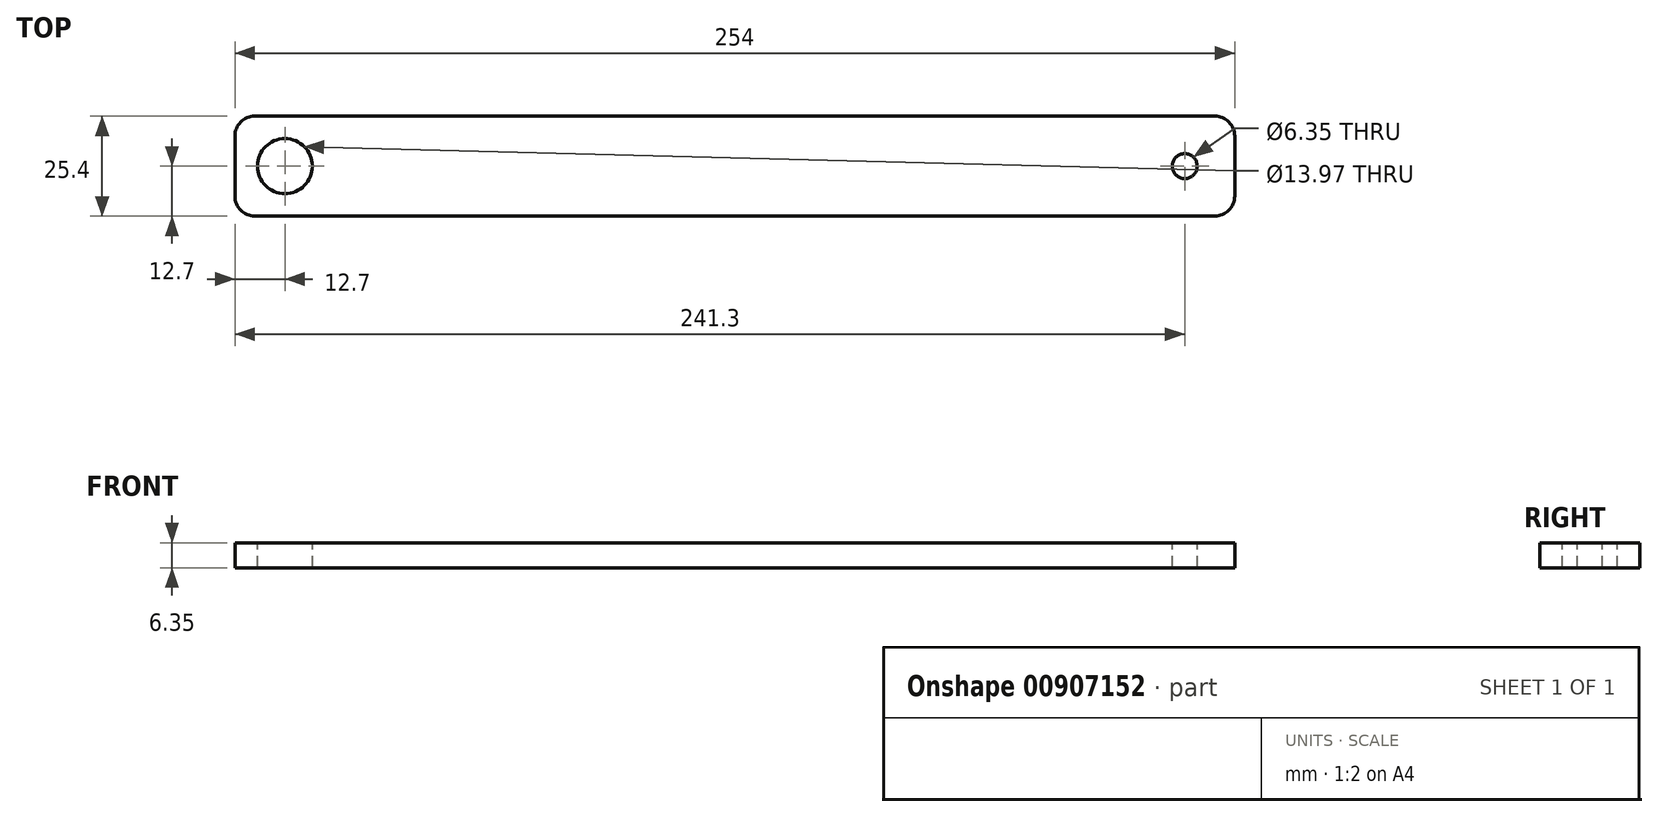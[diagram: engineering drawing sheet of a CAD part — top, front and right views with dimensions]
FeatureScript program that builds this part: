
annotation { "Feature Type Name" : "Feature", "Feature Type Description" : "" }
export const myFeature = defineFeature(function(context is Context, id is Id, definition is map)
    precondition{}
    {
        {
            var Q0;
            Q0=qCreatedBy(makeId("Front.planeOp"),FACE);
            var sketch = newSketch(context, id + "F0", { "sketchPlane" : qUnion([Q0])});
            skLineSegment(sketch, "E0.bottom", {"start": v(0, 0) * mm, "end": v(254, 0) * mm});
            skLineSegment(sketch, "E0.top", {"start": v(0, 6.35) * mm, "end": v(254, 6.35) * mm});
            skLineSegment(sketch, "E0.left", {"start": v(0, 0) * mm, "end": v(0, 6.35) * mm});
            skLineSegment(sketch, "E0.right", {"start": v(254, 0) * mm, "end": v(254, 6.35) * mm});
            skSolve(sketch);
        }
        {
            var Q0;
            Q0 = qSketchRegion(id + "F0", true);
            extrude(context, id + "F1", {"entities" : qUnion([Q0]), "oppositeDirection" : true, "depth" : 25.4 * mm, "offsetDistance" : 25.4 * mm});
        }
        {
            var Q0;
            Q0=makeQuery(id+"F1.opExtrude","SWEPT_FACE",FACE,{"disambiguationData":[OSD([sQuery(id+"F0.wireOp",EDGE,"E0.top")])]});
            var sketch = newSketch(context, id + "F2", { "sketchPlane" : qUnion([Q0])});
            skCircle(sketch, "E1", {"center": v(12.7, 12.7) * mm, "radius": 6.99 * mm});
            skPoint(sketch, "E1.centerSnap0", {"position": v(0, 12.7) * mm});
            skCircle(sketch, "E2", {"center": v(241.3, 12.7) * mm, "radius": 3.18 * mm});
            skSolve(sketch);
        }
        {
            var Q0;
            Q0 = qSketchRegion(id + "F2", true);
            extrude(context, id + "F3", {"entities" : qUnion([Q0]), "operationType" : NewBodyOperationType.REMOVE, "oppositeDirection" : true, "depth" : 25.4 * mm, "offsetDistance" : 25.4 * mm});
        }
        {
            var Q0;
            Q0=makeQuery(id+"F1.opExtrude","CAP_EDGE",EDGE,{"disambiguationData":[OSD([sQuery(id+"F0.wireOp",EDGE,"E0.right")])],"isStart":true});
            var Q1;
            Q1=makeQuery(id+"F1.opExtrude","CAP_EDGE",EDGE,{"disambiguationData":[OSD([sQuery(id+"F0.wireOp",EDGE,"E0.right")])],"isStart":false});
            var Q2;
            Q2=makeQuery(id+"F1.opExtrude","CAP_EDGE",EDGE,{"disambiguationData":[OSD([sQuery(id+"F0.wireOp",EDGE,"E0.left")])],"isStart":true});
            var Q3;
            Q3=makeQuery(id+"F1.opExtrude","CAP_EDGE",EDGE,{"disambiguationData":[OSD([sQuery(id+"F0.wireOp",EDGE,"E0.left")])],"isStart":false});
            fillet(context, id + "F4", {"entities" : qUnion([Q0, Q1, Q2, Q3]), "radius" : 5.08 * mm, "tangentPropagation" : true, "allowEdgeOverflow" : false});
        }
    });
